# Revit family: ThinAir_HAND_DRYER_with_HEPA_filter
name_source: partatom
category: Specialty Equipment
units: mm (PartAtom-declared; Revit-internal decimal feet)

## family parameters
Cut with Voids When Loaded = No
Host = Face
OmniClass Number = 23.40.20.21.14
OmniClass Title = Hand and Hair Dryers
Part Type = Normal
Room Calculation Point = No
Round Connector Dimension = Use Diameter
Shared = No

## types (3) — shared parameters
Air Temperature (Farenheit) = 141 °F
Cover Finish = Polymer - Excel Dryer  - ABS - White
Default Elevation = 3' - 3"
Depth = 0' - 4"
Description = ThinAir Series
Heating Element = 500 W
Height = 1' - 1 15/16"
Impact Resistant Note = UL 499
Keynote = 10 28 13
Manufacturer = Excel Dryer
Manufacturer Fax Number = 1-413-525-2853
Number of Poles = 1
Output at Outlet (LFM) = 16000 LFM
Phase = 1
Power Factor = 1
Product Documentation Link = https://www.exceldryer.com
Product Name = ThinAir Excel Dryer®With HEPA Filter
Product Page URL = http://www.exceldryer.com
Product Weight = 8 lbs
URL = http://www.exceldryer.com
Version = 2017 - v1.0b
Warranty Duration = 5 Years
Warranty URL = https://www.exceldryer.com
Width = 0' - 8 29/32"

## per-type parameters (varying)
| type | Amperage | Apparent Load | Assembly Code | Frequency | Voltage | Watts |
| TA-ABS-110-120V 7-7.7A - 770-915W | 8 A | 960 VA | C1090.4040 | 60 Hz | 120 V | 915 W |
| TA-ABS-208-277V 3.6-4A - 735-950W | 4 A | 984 VA | C1030200 | 60 Hz | 277 V | 950 W |
| TA-ABS-230V 3.9A 890W | 4 A | 920 VA | C1030200 | 50 Hz | 230 V | 890 W |

note: column(s) folded — value = type name in every type: Model

## geometry (parser evidence)
native form markers: Sweep x2
no freeform markers — native parametric forms only
